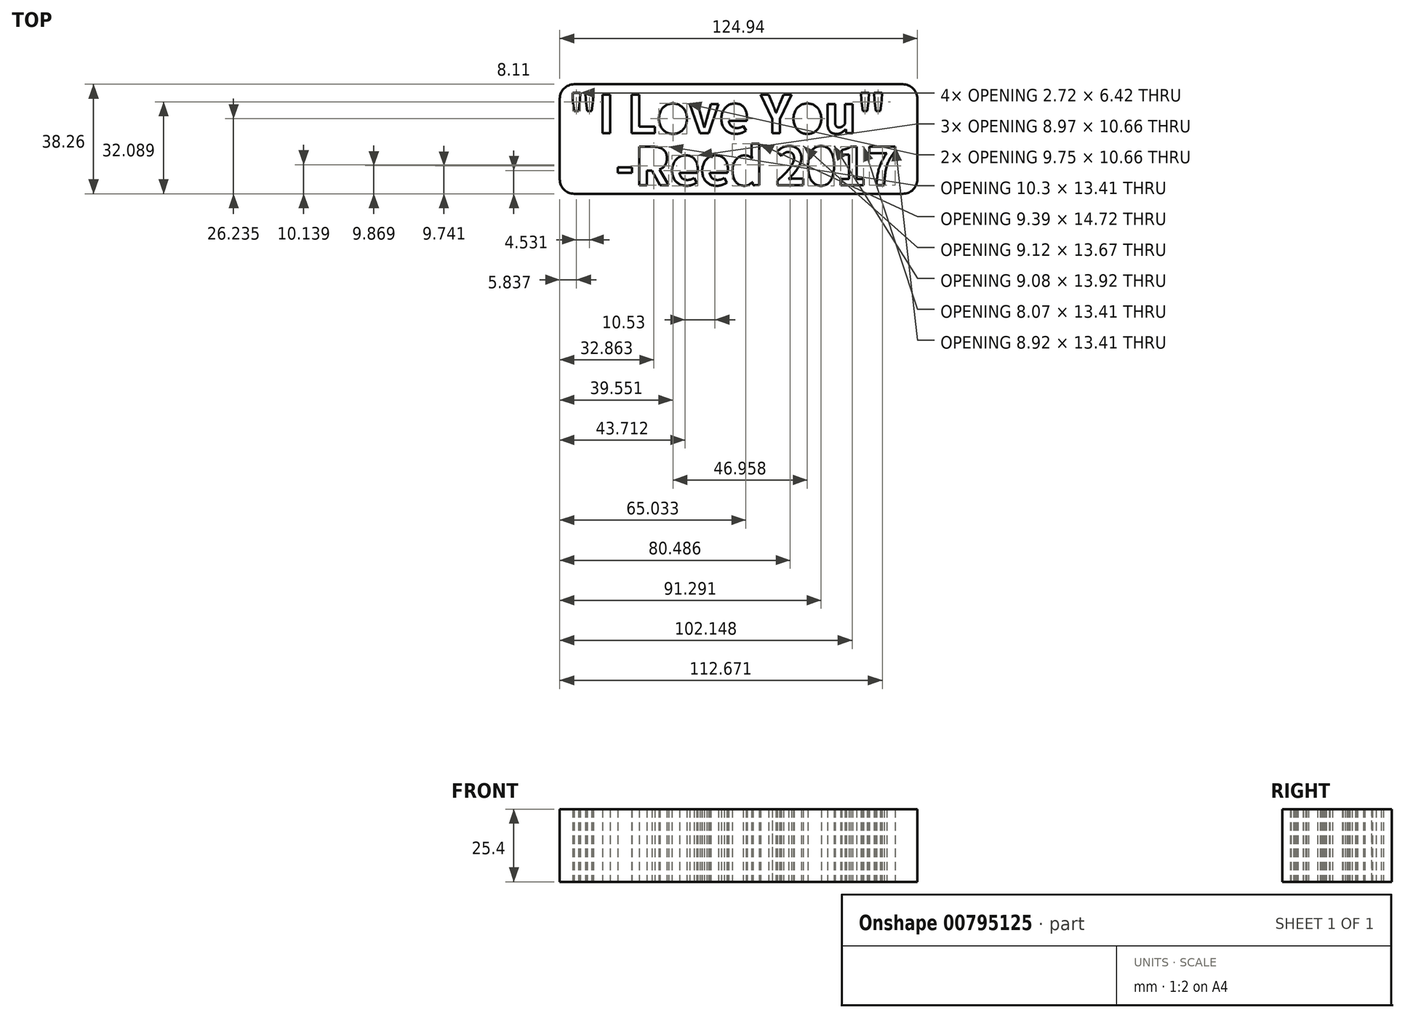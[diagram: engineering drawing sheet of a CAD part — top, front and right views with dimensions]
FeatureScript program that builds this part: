
annotation { "Feature Type Name" : "Feature", "Feature Type Description" : "" }
export const myFeature = defineFeature(function(context is Context, id is Id, definition is map)
    precondition{}
    {
        {
            var Q0;
            Q0=qCreatedBy(makeId("Top.planeOp"),FACE);
            var sketch = newSketch(context, id + "F0", { "sketchPlane" : qUnion([Q0])});
            skText(sketch, "E0", { "text": "\"I Love You\"\n    -Reed 2017", "fontName": "NotoSansCJKjp-Bold.otf"});
            skLineSegment(sketch, "E1.bottom", {"start": v(-52.47, 31.74) * mm, "end": v(72.47, 31.74) * mm});
            skLineSegment(sketch, "E1.top", {"start": v(-52.47, -6.52) * mm, "end": v(72.47, -6.52) * mm});
            skLineSegment(sketch, "E1.left", {"start": v(-52.47, 31.74) * mm, "end": v(-52.47, -6.52) * mm});
            skLineSegment(sketch, "E1.right", {"start": v(72.47, 31.74) * mm, "end": v(72.47, -6.52) * mm});
            const initialGuessF0  = {"E0": [-0.04957, 0.01464, 1, 0, 0.01305]};
            skSetInitialGuess(sketch, initialGuessF0);
            skSolve(sketch);
        }
        {
            var Q0;
            Q0=makeQuery(id+"F0.imprint","IMPRINT",FACE,{"disambiguationData":[TD([[makeQuery(id+"F0.imprint","IMPRINT",EDGE,{"derivedFrom":sQuery(id+"F0.wireOp",EDGE,"E0.sketch_text.stroke-0")}),-1.0]])]});
            extrude(context, id + "F1", {"entities" : qUnion([Q0]), "depth" : 25.4 * mm, "offsetDistance" : 25.4 * mm});
        }
        {
            var Q0;
            Q0=makeQuery(id+"F1.opExtrude","SWEPT_EDGE",EDGE,{"disambiguationData":[OSD([sQuery(id+"F0.wireOp",EDGE,"E1.top"),sQuery(id+"F0.wireOp",EDGE,"E1.left")])]});
            var Q1;
            Q1=makeQuery(id+"F1.opExtrude","SWEPT_EDGE",EDGE,{"disambiguationData":[OSD([sQuery(id+"F0.wireOp",EDGE,"E1.bottom"),sQuery(id+"F0.wireOp",EDGE,"E1.left")])]});
            var Q2;
            Q2=makeQuery(id+"F1.opExtrude","SWEPT_EDGE",EDGE,{"disambiguationData":[OSD([sQuery(id+"F0.wireOp",EDGE,"E1.top"),sQuery(id+"F0.wireOp",EDGE,"E1.right")])]});
            var Q3;
            Q3=makeQuery(id+"F1.opExtrude","SWEPT_EDGE",EDGE,{"disambiguationData":[OSD([sQuery(id+"F0.wireOp",EDGE,"E1.bottom"),sQuery(id+"F0.wireOp",EDGE,"E1.right")])]});
            fillet(context, id + "F2", {"entities" : qUnion([Q0, Q1, Q2, Q3]), "radius" : 5.08 * mm, "tangentPropagation" : true, "allowEdgeOverflow" : false});
        }
    });
